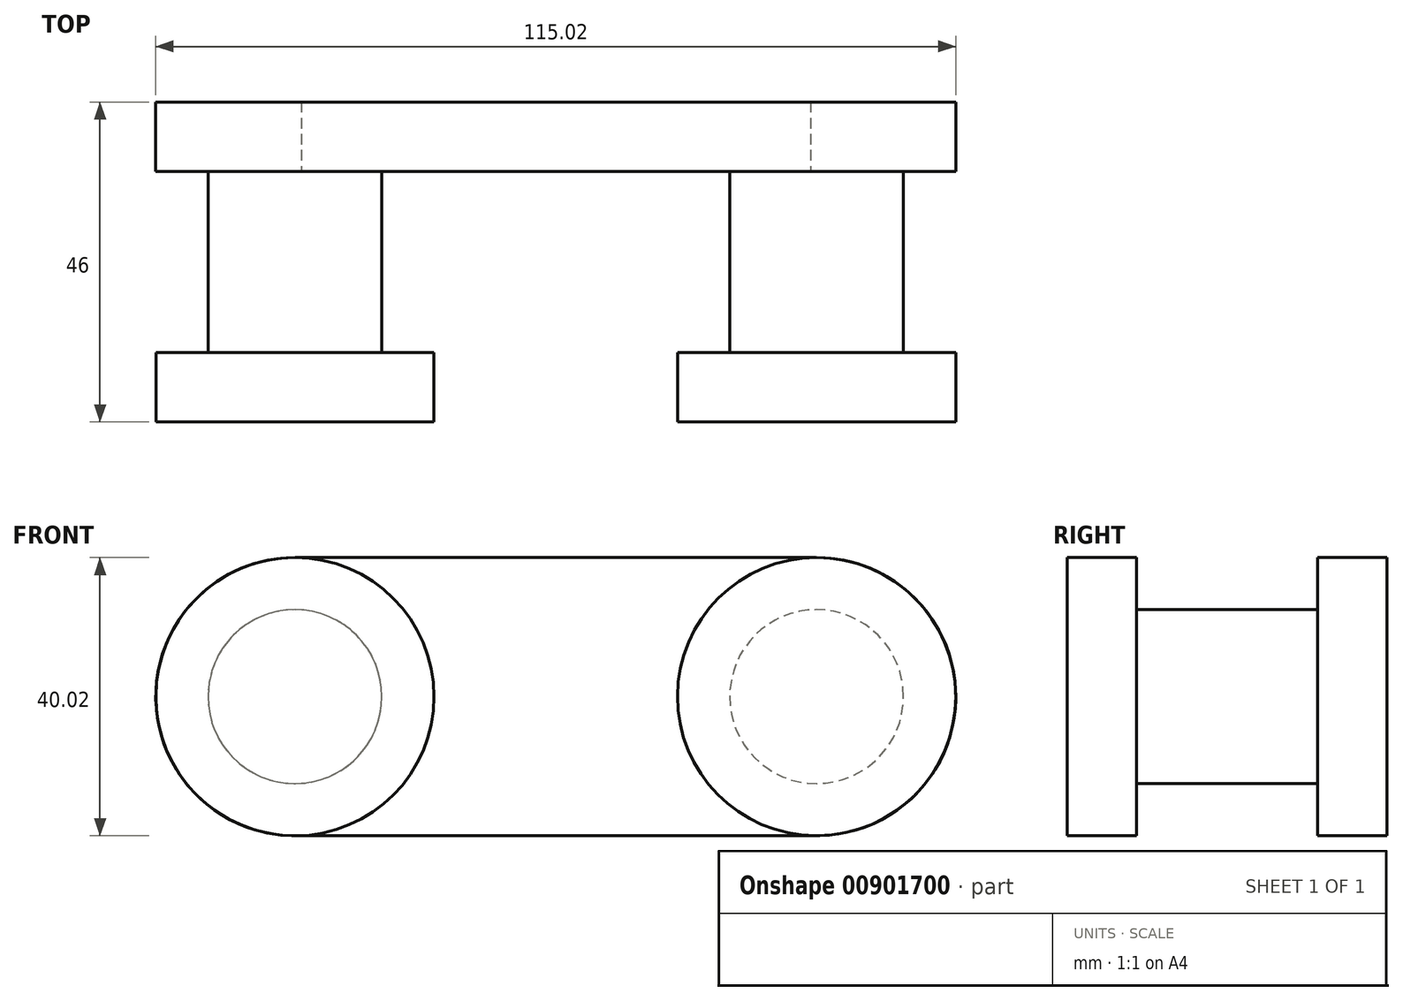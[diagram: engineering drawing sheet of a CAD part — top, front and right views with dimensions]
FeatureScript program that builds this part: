
annotation { "Feature Type Name" : "Feature", "Feature Type Description" : "" }
export const myFeature = defineFeature(function(context is Context, id is Id, definition is map)
    precondition{}
    {
        {
            var Q0;
            Q0=qCreatedBy(makeId("Front.planeOp"),FACE);
            var sketch = newSketch(context, id + "F0", { "sketchPlane" : qUnion([Q0])});
            skCircle(sketch, "E0", {"center": v(-37.5, 0) * mm, "radius": 20 * mm});
            skCircle(sketch, "E1", {"center": v(37.5, 0) * mm, "radius": 20 * mm});
            skLineSegment(sketch, "E2", {"start": v(-37.53, 20) * mm, "end": v(37.47, 20) * mm});
            skLineSegment(sketch, "E3", {"start": v(-37.35, -20) * mm, "end": v(37.65, -20) * mm});
            skSolve(sketch);
        }
        {
            var Q0;
            {var subQ0=sQuery(id+"F0.wireOp",EDGE,"E2");Q0=makeQuery(id+"F0.imprint","IMPRINT",FACE,{"disambiguationData":[TD([[makeQuery(id+"F0.imprint","IMPRINT",EDGE,{"derivedFrom":subQ0}),-1.0]])]});}
            var Q1;
            {var subQ0=sQuery(id+"F0.wireOp",EDGE,"E0");var subQ1=makeQuery(id+"F0.imprint","INTERSECT",VERTEX,{"derivedFrom":[subQ0,sQuery(id+"F0.wireOp",EDGE,"E2")]});Q1=makeQuery(id+"F0.imprint","IMPRINT",FACE,{"disambiguationData":[TD([[makeQuery(id+"F0.imprint","IMPRINT",EDGE,{"disambiguationData":[TD([[subQ1,-1.0]])],"derivedFrom":subQ0}),1.0]])]});}
            var Q2;
            {var subQ0=sQuery(id+"F0.wireOp",EDGE,"E1");var subQ1=makeQuery(id+"F0.imprint","INTERSECT",VERTEX,{"derivedFrom":[subQ0,sQuery(id+"F0.wireOp",EDGE,"E2")]});Q2=makeQuery(id+"F0.imprint","IMPRINT",FACE,{"disambiguationData":[TD([[makeQuery(id+"F0.imprint","IMPRINT",EDGE,{"disambiguationData":[TD([[subQ1,-1.0]])],"derivedFrom":subQ0}),1.0]])]});}
            extrude(context, id + "F1", {"entities" : qUnion([Q0, Q1, Q2]), "depth" : 10 * mm, "offsetDistance" : 25 * mm});
        }
        {
            var Q0;
            {var subQ0=sQuery(id+"F0.wireOp",EDGE,"E1");var subQ1=makeQuery(id+"F0.imprint","INTERSECT",VERTEX,{"derivedFrom":[subQ0,sQuery(id+"F0.wireOp",EDGE,"E2")]});Q0=makeQuery(id+"F0.imprint","IMPRINT",FACE,{"disambiguationData":[TD([[makeQuery(id+"F0.imprint","IMPRINT",EDGE,{"disambiguationData":[TD([[subQ1,-1.0]])],"derivedFrom":subQ0}),1.0]])]});}
            var sketch = newSketch(context, id + "F2", { "sketchPlane" : qUnion([Q0])});
            skCircle(sketch, "E4", {"center": v(37.5, 0) * mm, "radius": 12.5 * mm});
            skCircle(sketch, "E5.MirrorC", {"center": v(-37.5, 0) * mm, "radius": 12.5 * mm});
            skSolve(sketch);
        }
        {
            var Q0;
            Q0 = qSketchRegion(id + "F2", true);
            extrude(context, id + "F3", {"entities" : qUnion([Q0]), "operationType" : NewBodyOperationType.ADD, "oppositeDirection" : true, "depth" : 26 * mm, "offsetDistance" : 25 * mm});
        }
        {
            var Q0;
            Q0=makeQuery(id+"F3.opExtrude","CAP_FACE",FACE,{"disambiguationData":[OSD([sQuery(id+"F2.wireOp",EDGE,"E4")])],"isStart":false});
            var sketch = newSketch(context, id + "F4", { "sketchPlane" : qUnion([Q0])});
            skCircle(sketch, "E6", {"center": v(-37.5, 0) * mm, "radius": 20 * mm});
            skCircle(sketch, "E7.MirrorC", {"center": v(37.5, 0) * mm, "radius": 20 * mm});
            skLineSegment(sketch, "E8", {"start": v(-37.4, 20) * mm, "end": v(37.4, 20) * mm});
            skLineSegment(sketch, "E9", {"start": v(-38.4, -19.99) * mm, "end": v(36.6, -19.99) * mm});
            skSolve(sketch);
        }
        {
            var Q0;
            Q0 = qSketchRegion(id + "F4", true);
            extrude(context, id + "F5", {"entities" : qUnion([Q0]), "operationType" : NewBodyOperationType.ADD, "depth" : 10 * mm, "offsetDistance" : 25 * mm});
        }
    });
